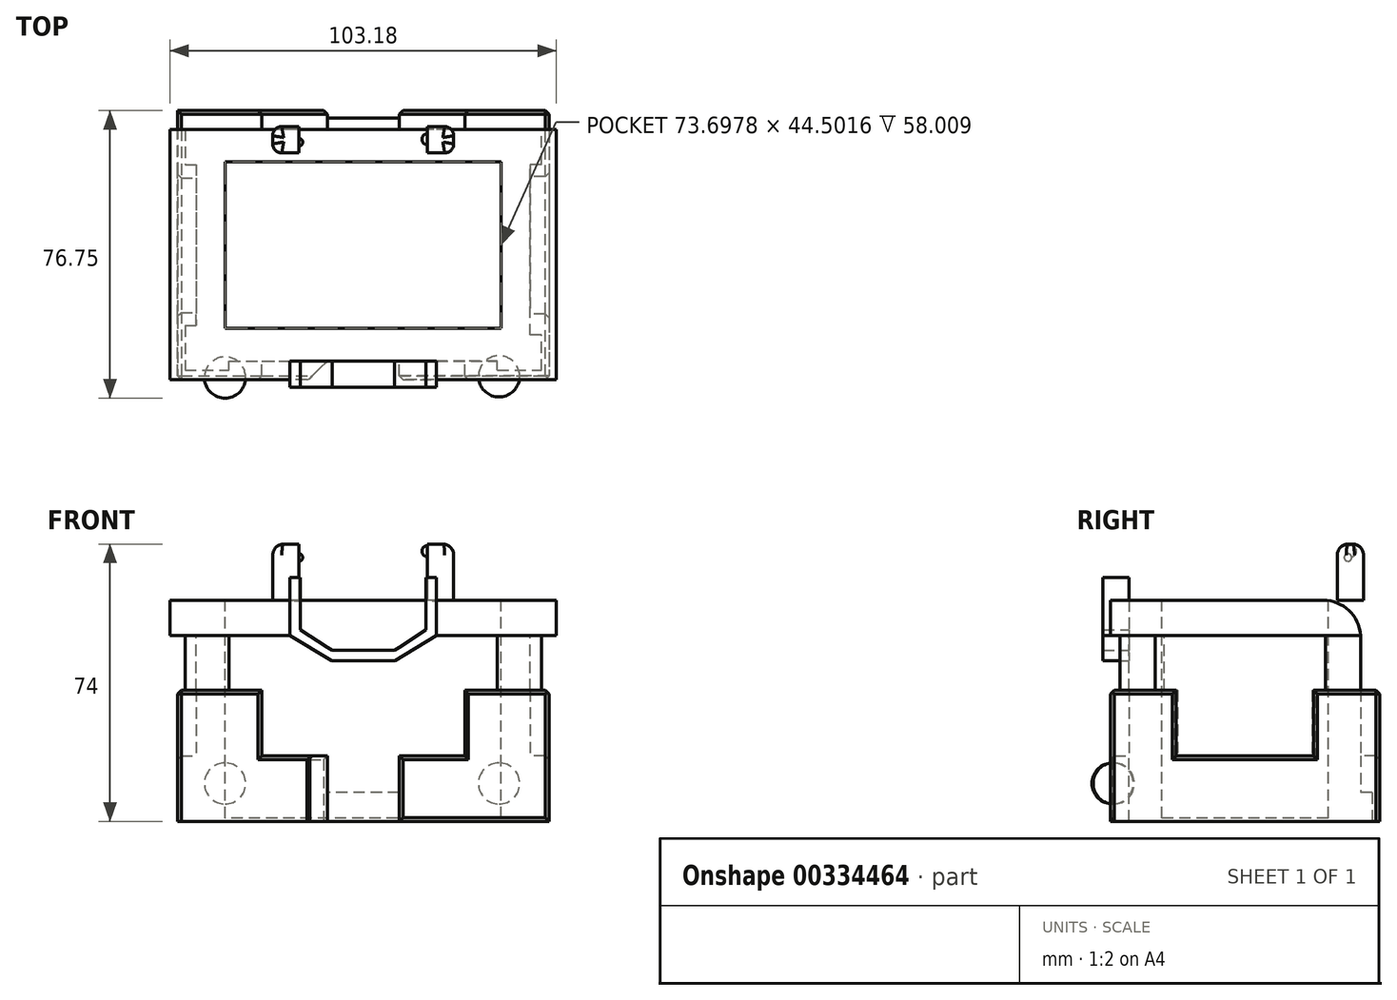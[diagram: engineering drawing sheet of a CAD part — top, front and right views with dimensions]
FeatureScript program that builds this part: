
annotation { "Feature Type Name" : "Feature", "Feature Type Description" : "" }
export const myFeature = defineFeature(function(context is Context, id is Id, definition is map)
    precondition{}
    {
        {
            var Q0;
            Q0=qCreatedBy(makeId("Top.planeOp"),FACE);
            var sketch = newSketch(context, id + "F0", { "sketchPlane" : qUnion([Q0])});
            skLineSegment(sketch, "E0.bottom", {"start": v(44.6, 30.9) * mm, "end": v(-44.6, 30.9) * mm});
            skLineSegment(sketch, "E0.top", {"start": v(44.6, -30.9) * mm, "end": v(-44.6, -30.9) * mm});
            skLineSegment(sketch, "E0.left", {"start": v(44.6, 30.9) * mm, "end": v(44.6, -30.9) * mm});
            skLineSegment(sketch, "E0.right", {"start": v(-44.6, 30.9) * mm, "end": v(-44.6, -30.9) * mm});
            skPoint(sketch, "E0.middle", {"position": v(0, 0) * mm});
            skSolve(sketch);
        }
        {
            var Q0;
            Q0 = qSketchRegion(id + "F0", true);
            extrude(context, id + "F1", {"entities" : qUnion([Q0]), "depth" : 59 * mm});
        }
        {
            var Q0;
            Q0=makeQuery(id+"F1.opExtrude","CAP_FACE",FACE,{"disambiguationData":[OSD([sQuery(id+"F0.wireOp",EDGE,"E0.bottom"),sQuery(id+"F0.wireOp",EDGE,"E0.top"),sQuery(id+"F0.wireOp",EDGE,"E0.left"),sQuery(id+"F0.wireOp",EDGE,"E0.right")])],"isStart":false});
            var sketch = newSketch(context, id + "F2", { "sketchPlane" : qUnion([Q0])});
            skLineSegment(sketch, "E1.bottom", {"start": v(36.85, 22.25) * mm, "end": v(-36.85, 22.25) * mm});
            skLineSegment(sketch, "E1.top", {"start": v(36.85, -22.25) * mm, "end": v(-36.85, -22.25) * mm});
            skLineSegment(sketch, "E1.left", {"start": v(36.85, 22.25) * mm, "end": v(36.85, -22.25) * mm});
            skLineSegment(sketch, "E1.right", {"start": v(-36.85, 22.25) * mm, "end": v(-36.85, -22.25) * mm});
            skPoint(sketch, "E1.middle", {"position": v(0, 0) * mm});
            skSolve(sketch);
        }
        {
            var Q0;
            Q0=makeQuery(id+"F2.imprint","IMPRINT",FACE,{"disambiguationData":[TD([[makeQuery(id+"F2.imprint","IMPRINT",EDGE,{"derivedFrom":sQuery(id+"F2.wireOp",EDGE,"E1.bottom")}),1.0]])]});
            extrude(context, id + "F3", {"entities" : qUnion([Q0]), "operationType" : NewBodyOperationType.REMOVE, "oppositeDirection" : true, "depth" : 58.1 * mm});
        }
        {
            var Q0;
            Q0=makeQuery(id+"F1.opExtrude","SWEPT_FACE",FACE,{"disambiguationData":[OSD([sQuery(id+"F0.wireOp",EDGE,"E0.top")])]});
            var sketch = newSketch(context, id + "F4", { "sketchPlane" : qUnion([Q0])});
            skLineSegment(sketch, "E2", {"start": v(-19.54, 65.05) * mm, "end": v(-19.54, 49.66) * mm});
            skLineSegment(sketch, "E3", {"start": v(-19.54, 49.66) * mm, "end": v(-8.44, 42.84) * mm});
            skLineSegment(sketch, "E4", {"start": v(-8.44, 42.84) * mm, "end": v(0, 42.84) * mm});
            skLineSegment(sketch, "E5.MirrorCS", {"start": v(8.44, 42.84) * mm, "end": v(0, 42.84) * mm});
            skLineSegment(sketch, "E6.MirrorCS", {"start": v(19.54, 49.66) * mm, "end": v(8.44, 42.84) * mm});
            skLineSegment(sketch, "E7.MirrorCS", {"start": v(19.54, 65.05) * mm, "end": v(19.54, 49.66) * mm});
            skLineSegment(sketch, "E8", {"start": v(-19.54, 65.05) * mm, "end": v(-16.74, 65.05) * mm});
            skLineSegment(sketch, "E9", {"start": v(-16.74, 65.05) * mm, "end": v(-16.74, 53.05) * mm});
            skLineSegment(sketch, "E10", {"start": v(-16.74, 53.05) * mm, "end": v(-16.74, 51.18) * mm});
            skLineSegment(sketch, "E11", {"start": v(-16.74, 51.18) * mm, "end": v(-9.6, 46.48) * mm});
            skLineSegment(sketch, "E12", {"start": v(-9.6, 46.48) * mm, "end": v(-8.32, 45.64) * mm});
            skLineSegment(sketch, "E13", {"start": v(-8.32, 45.64) * mm, "end": v(0, 45.64) * mm});
            skLineSegment(sketch, "E14.MirrorCS", {"start": v(8.32, 45.64) * mm, "end": v(0, 45.64) * mm});
            skLineSegment(sketch, "E15.MirrorCS", {"start": v(16.74, 51.18) * mm, "end": v(9.6, 46.48) * mm});
            skLineSegment(sketch, "E16.MirrorCS", {"start": v(9.6, 46.48) * mm, "end": v(8.32, 45.64) * mm});
            skLineSegment(sketch, "E17.MirrorCS", {"start": v(16.74, 65.05) * mm, "end": v(16.74, 53.05) * mm});
            skLineSegment(sketch, "E18.MirrorCS", {"start": v(16.74, 53.05) * mm, "end": v(16.74, 51.18) * mm});
            skLineSegment(sketch, "E19.MirrorCS", {"start": v(19.54, 65.05) * mm, "end": v(16.74, 65.05) * mm});
            skLineSegment(sketch, "E20.bottom", {"start": v(-44.6, 0) * mm, "end": v(-9.6, 0) * mm});
            skLineSegment(sketch, "E20.top", {"start": v(-44.6, 35) * mm, "end": v(-27.1, 35) * mm});
            skLineSegment(sketch, "E20.left", {"start": v(-44.6, 0) * mm, "end": v(-44.6, 35) * mm});
            skLineSegment(sketch, "E20.right", {"start": v(-9.6, 0) * mm, "end": v(-9.6, 17.5) * mm});
            skLineSegment(sketch, "E21.bottom", {"start": v(44.6, 0) * mm, "end": v(9.6, 0) * mm});
            skLineSegment(sketch, "E21.top", {"start": v(44.6, 35) * mm, "end": v(27.1, 35) * mm});
            skLineSegment(sketch, "E21.left", {"start": v(44.6, 0) * mm, "end": v(44.6, 35) * mm});
            skLineSegment(sketch, "E21.right", {"start": v(9.6, 0) * mm, "end": v(9.6, 17.5) * mm});
            skLineSegment(sketch, "E22", {"start": v(-27.1, 35) * mm, "end": v(-27.1, 17.5) * mm});
            skPoint(sketch, "E22.endSnap0", {"position": v(-9.6, 17.5) * mm});
            skLineSegment(sketch, "E23", {"start": v(-27.1, 17.5) * mm, "end": v(-9.6, 17.5) * mm});
            skLineSegment(sketch, "E24", {"start": v(27.1, 35) * mm, "end": v(27.1, 17.5) * mm});
            skLineSegment(sketch, "E25", {"start": v(27.1, 17.5) * mm, "end": v(9.6, 17.5) * mm});
            skPoint(sketch, "E26.orphan", {"position": v(9.6, 35) * mm});
            skPoint(sketch, "E27.orphan", {"position": v(-9.6, 35) * mm});
            skLineSegment(sketch, "E28", {"start": v(-9.6, 0) * mm, "end": v(9.6, 0) * mm});
            skLineSegment(sketch, "E29", {"start": v(-9.6, 7.65) * mm, "end": v(9.6, 7.65) * mm});
            skLineSegment(sketch, "E30", {"start": v(19.54, 49.66) * mm, "end": v(44.6, 49.66) * mm});
            skLineSegment(sketch, "E31", {"start": v(44.6, 49.66) * mm, "end": v(44.6, 59) * mm});
            skLineSegment(sketch, "E32", {"start": v(44.6, 59) * mm, "end": v(19.54, 59) * mm});
            skLineSegment(sketch, "E33", {"start": v(-44.6, 59) * mm, "end": v(-19.54, 59) * mm});
            skLineSegment(sketch, "E34", {"start": v(-19.54, 59) * mm, "end": v(-19.54, 49.66) * mm});
            skLineSegment(sketch, "E35", {"start": v(-44.6, 49.66) * mm, "end": v(-44.6, 59) * mm});
            skLineSegment(sketch, "E36", {"start": v(-44.6, 49.66) * mm, "end": v(-19.54, 49.66) * mm});
            skLineSegment(sketch, "E37", {"start": v(-35.84, 35) * mm, "end": v(-35.84, 49.66) * mm});
            skLineSegment(sketch, "E38", {"start": v(35.84, 35) * mm, "end": v(35.84, 49.66) * mm});
            skSolve(sketch);
        }
        {
            var Q0;
            {var subQ4=sQuery(id+"F4.wireOp",EDGE,"E21.bottom");Q0=makeQuery(id+"F4.imprint","IMPRINT",FACE,{"disambiguationData":[TD([[makeQuery(id+"F4.imprint","IMPRINT",EDGE,{"derivedFrom":subQ4}),-1.0]])]});}
            var Q1;
            {var subQ5=sQuery(id+"F4.wireOp",EDGE,"E20.bottom");Q1=makeQuery(id+"F4.imprint","IMPRINT",FACE,{"disambiguationData":[TD([[makeQuery(id+"F4.imprint","IMPRINT",EDGE,{"derivedFrom":subQ5}),-1.0]])]});}
            extrude(context, id + "F5", {"entities" : qUnion([Q0, Q1]), "operationType" : NewBodyOperationType.ADD, "depth" : 5 * mm});
        }
        {
            var Q0;
            Q0=makeQuery(id+"F4.imprint","IMPRINT",FACE,{"disambiguationData":[TD([[makeQuery(id+"F4.imprint","IMPRINT",EDGE,{"derivedFrom":sQuery(id+"F4.wireOp",EDGE,"E33")}),1.0]])]});
            var Q1;
            {var subQ0=sQuery(id+"F4.wireOp",EDGE,"E31");Q1=makeQuery(id+"F4.imprint","IMPRINT",FACE,{"disambiguationData":[TD([[makeQuery(id+"F4.imprint","IMPRINT",EDGE,{"derivedFrom":subQ0}),-1.0]])]});}
            extrude(context, id + "F6", {"entities" : qUnion([Q0, Q1]), "operationType" : NewBodyOperationType.ADD, "depth" : 5 * mm});
        }
        {
            var Q0;
            Q0=makeQuery(id+"F4.imprint","IMPRINT",FACE,{"disambiguationData":[TD([[makeQuery(id+"F4.imprint","IMPRINT",EDGE,{"derivedFrom":sQuery(id+"F4.wireOp",EDGE,"E3")}),1.0]])]});
            var Q1;
            {var subQ0=sQuery(id+"F4.wireOp",EDGE,"E2");Q1=makeQuery(id+"F4.imprint","IMPRINT",FACE,{"disambiguationData":[TD([[makeQuery(id+"F4.imprint","IMPRINT",EDGE,{"derivedFrom":subQ0}),1.0]])]});}
            var Q2;
            {var subQ0=sQuery(id+"F4.wireOp",EDGE,"E19.MirrorCS");Q2=makeQuery(id+"F4.imprint","IMPRINT",FACE,{"disambiguationData":[TD([[makeQuery(id+"F4.imprint","IMPRINT",EDGE,{"derivedFrom":subQ0}),1.0]])]});}
            extrude(context, id + "F7", {"entities" : qUnion([Q0, Q1, Q2]), "operationType" : NewBodyOperationType.ADD, "depth" : 7 * mm});
        }
        {
            var Q0;
            Q0=makeQuery(id+"F1.opExtrude","SWEPT_FACE",FACE,{"disambiguationData":[OSD([sQuery(id+"F0.wireOp",EDGE,"E0.bottom")])]});
            var sketch = newSketch(context, id + "F8", { "sketchPlane" : qUnion([Q0])});
            skLineSegment(sketch, "E39.0.0", {"start": v(-9.6, 17.5) * mm, "end": v(-9.6, 0) * mm});
            skLineSegment(sketch, "E39.0.1", {"start": v(-9.6, 0) * mm, "end": v(-44.6, 0) * mm});
            skLineSegment(sketch, "E39.0.2", {"start": v(-44.6, 0) * mm, "end": v(-44.6, 35) * mm});
            skLineSegment(sketch, "E39.0.3", {"start": v(-44.6, 35) * mm, "end": v(-27.1, 35) * mm});
            skLineSegment(sketch, "E39.0.4", {"start": v(-27.1, 35) * mm, "end": v(-27.1, 17.5) * mm});
            skLineSegment(sketch, "E39.0.5", {"start": v(-27.1, 17.5) * mm, "end": v(-9.6, 17.5) * mm});
            skLineSegment(sketch, "E40.0.0", {"start": v(-35.84, 49.66) * mm, "end": v(-35.84, 35) * mm});
            skLineSegment(sketch, "E40.0.1", {"start": v(-35.84, 35) * mm, "end": v(-44.6, 35) * mm});
            skLineSegment(sketch, "E40.0.2", {"start": v(-44.6, 35) * mm, "end": v(-44.6, 49.66) * mm});
            skLineSegment(sketch, "E40.0.3", {"start": v(-44.6, 49.66) * mm, "end": v(-35.84, 49.66) * mm});
            skLineSegment(sketch, "E41.0.0", {"start": v(-19.54, 59) * mm, "end": v(-19.54, 49.66) * mm});
            skLineSegment(sketch, "E41.0.1", {"start": v(-19.54, 49.66) * mm, "end": v(-44.6, 49.66) * mm});
            skLineSegment(sketch, "E41.0.2", {"start": v(-44.6, 49.66) * mm, "end": v(-44.6, 59) * mm});
            skLineSegment(sketch, "E41.0.3", {"start": v(-44.6, 59) * mm, "end": v(-19.54, 59) * mm});
            skLineSegment(sketch, "E42.0.0", {"start": v(-19.54, 49.66) * mm, "end": v(-19.54, 65.05) * mm});
            skLineSegment(sketch, "E42.0.1", {"start": v(-19.54, 65.05) * mm, "end": v(-16.74, 65.05) * mm});
            skLineSegment(sketch, "E42.0.2", {"start": v(-16.74, 65.05) * mm, "end": v(-16.74, 51.18) * mm});
            skLineSegment(sketch, "E42.0.3", {"start": v(-16.74, 51.18) * mm, "end": v(-9.6, 46.48) * mm});
            skLineSegment(sketch, "E42.0.4", {"start": v(-9.6, 46.48) * mm, "end": v(-8.32, 45.64) * mm});
            skLineSegment(sketch, "E42.0.5", {"start": v(-8.32, 45.64) * mm, "end": v(8.32, 45.64) * mm});
            skLineSegment(sketch, "E42.0.6", {"start": v(8.32, 45.64) * mm, "end": v(9.6, 46.48) * mm});
            skLineSegment(sketch, "E42.0.7", {"start": v(9.6, 46.48) * mm, "end": v(16.74, 51.18) * mm});
            skLineSegment(sketch, "E42.0.8", {"start": v(16.74, 51.18) * mm, "end": v(16.74, 65.05) * mm});
            skLineSegment(sketch, "E42.0.9", {"start": v(16.74, 65.05) * mm, "end": v(19.54, 65.05) * mm});
            skLineSegment(sketch, "E42.0.10", {"start": v(19.54, 65.05) * mm, "end": v(19.54, 49.66) * mm});
            skLineSegment(sketch, "E42.0.11", {"start": v(19.54, 49.66) * mm, "end": v(8.44, 42.84) * mm});
            skLineSegment(sketch, "E42.0.12", {"start": v(8.44, 42.84) * mm, "end": v(-8.44, 42.84) * mm});
            skLineSegment(sketch, "E42.0.13", {"start": v(-8.44, 42.84) * mm, "end": v(-19.54, 49.66) * mm});
            skLineSegment(sketch, "E43.0.0", {"start": v(44.6, 59) * mm, "end": v(44.6, 49.66) * mm});
            skLineSegment(sketch, "E43.0.1", {"start": v(44.6, 49.66) * mm, "end": v(19.54, 49.66) * mm});
            skLineSegment(sketch, "E43.0.2", {"start": v(19.54, 49.66) * mm, "end": v(19.54, 59) * mm});
            skLineSegment(sketch, "E43.0.3", {"start": v(19.54, 59) * mm, "end": v(44.6, 59) * mm});
            skLineSegment(sketch, "E44.0.0", {"start": v(44.6, 35) * mm, "end": v(35.84, 35) * mm});
            skLineSegment(sketch, "E44.0.1", {"start": v(35.84, 35) * mm, "end": v(35.84, 49.66) * mm});
            skLineSegment(sketch, "E44.0.2", {"start": v(35.84, 49.66) * mm, "end": v(44.6, 49.66) * mm});
            skLineSegment(sketch, "E44.0.3", {"start": v(44.6, 49.66) * mm, "end": v(44.6, 35) * mm});
            skLineSegment(sketch, "E45.0.0", {"start": v(44.6, 0) * mm, "end": v(9.6, 0) * mm});
            skLineSegment(sketch, "E45.0.1", {"start": v(9.6, 0) * mm, "end": v(9.6, 17.5) * mm});
            skLineSegment(sketch, "E45.0.2", {"start": v(9.6, 17.5) * mm, "end": v(27.1, 17.5) * mm});
            skLineSegment(sketch, "E45.0.3", {"start": v(27.1, 17.5) * mm, "end": v(27.1, 35) * mm});
            skLineSegment(sketch, "E45.0.4", {"start": v(27.1, 35) * mm, "end": v(44.6, 35) * mm});
            skLineSegment(sketch, "E45.0.5", {"start": v(44.6, 35) * mm, "end": v(44.6, 0) * mm});
            skLineSegment(sketch, "E46.0.0", {"start": v(-9.6, 7.65) * mm, "end": v(9.6, 7.65) * mm});
            skLineSegment(sketch, "E46.0.1", {"start": v(9.6, 7.65) * mm, "end": v(9.6, 0) * mm});
            skLineSegment(sketch, "E46.0.2", {"start": v(9.6, 0) * mm, "end": v(-9.6, 0) * mm});
            skLineSegment(sketch, "E46.0.3", {"start": v(-9.6, 0) * mm, "end": v(-9.6, 7.65) * mm});
            skLineSegment(sketch, "E47", {"start": v(0, 0) * mm, "end": v(0, 73.71) * mm});
            skArc(sketch, "E48", {"start": v(-63.35, 14.4) * mm, "mid": v(-68.85, 8.9) * mm, "end": v(-63.35, 3.4) * mm});
            skArc(sketch, "E49", {"start": v(55.37, 14.4) * mm, "mid": v(49.87, 8.9) * mm, "end": v(55.37, 3.4) * mm});
            skLineSegment(sketch, "E50", {"start": v(-63.35, 3.4) * mm, "end": v(-63.35, 14.4) * mm});
            skLineSegment(sketch, "E51", {"start": v(55.37, 3.4) * mm, "end": v(55.37, 14.4) * mm});
            skSolve(sketch);
        }
        {
            var Q0;
            Q0=makeQuery(id+"F8.imprint","IMPRINT",FACE,{"disambiguationData":[TD([[makeQuery(id+"F8.imprint","IMPRINT",EDGE,{"derivedFrom":sQuery(id+"F8.wireOp",EDGE,"E45.0.0")}),1.0]])]});
            var Q1;
            Q1=makeQuery(id+"F8.imprint","IMPRINT",FACE,{"disambiguationData":[TD([[makeQuery(id+"F8.imprint","IMPRINT",EDGE,{"derivedFrom":sQuery(id+"F8.wireOp",EDGE,"E39.0.0")}),-1.0]])]});
            extrude(context, id + "F9", {"entities" : qUnion([Q0, Q1]), "operationType" : NewBodyOperationType.ADD, "depth" : 5 * mm});
        }
        {
            var Q0;
            Q0=makeQuery(id+"F8.imprint","IMPRINT",FACE,{"disambiguationData":[TD([[makeQuery(id+"F8.imprint","IMPRINT",EDGE,{"derivedFrom":sQuery(id+"F8.wireOp",EDGE,"E46.0.0")}),-1.0]])]});
            extrude(context, id + "F10", {"entities" : qUnion([Q0]), "operationType" : NewBodyOperationType.ADD, "depth" : 3 * mm});
        }
        {
            var Q0;
            {var subQ3=sQuery(id+"F4.wireOp",EDGE,"E37");Q0=makeQuery(id+"F4.imprint","IMPRINT",FACE,{"disambiguationData":[TD([[makeQuery(id+"F4.imprint","IMPRINT",EDGE,{"derivedFrom":subQ3}),1.0]])]});}
            var Q1;
            {var subQ3=sQuery(id+"F4.wireOp",EDGE,"E38");Q1=makeQuery(id+"F4.imprint","IMPRINT",FACE,{"disambiguationData":[TD([[makeQuery(id+"F4.imprint","IMPRINT",EDGE,{"derivedFrom":subQ3}),-1.0]])]});}
            extrude(context, id + "F11", {"entities" : qUnion([Q0, Q1]), "operationType" : NewBodyOperationType.ADD, "depth" : 2.5 * mm});
        }
        {
            var Q0;
            {var subQ0=sQuery(id+"F0.wireOp",EDGE,"E0.right");Q0=makeQuery(id+"F11.boolean.opBoolean","MERGE",FACE,{"derivedFrom":[makeQuery(id+"F9.boolean.opBoolean","MERGE",FACE,{"derivedFrom":[makeQuery(id+"F6.boolean.opBoolean","MERGE",FACE,{"derivedFrom":[makeQuery(id+"F5.boolean.opBoolean","MERGE",FACE,{"derivedFrom":[makeQuery(id+"F1.opExtrude","SWEPT_FACE",FACE,{"disambiguationData":[OSD([subQ0])]}),makeQuery(id+"F5.opExtrude","SWEPT_FACE",FACE,{"disambiguationData":[OSD([sQuery(id+"F4.wireOp",EDGE,"E20.left")])]})]}),makeQuery(id+"F6.opExtrude","SWEPT_FACE",FACE,{"disambiguationData":[OSD([sQuery(id+"F4.wireOp",EDGE,"E35")])]})]}),makeQuery(id+"F9.opExtrude","SWEPT_FACE",FACE,{"disambiguationData":[OSD([sQuery(id+"F8.wireOp",EDGE,"E45.0.5")])]})]}),makeQuery(id+"F11.opExtrude","SWEPT_FACE",FACE,{"disambiguationData":[OSD([sQuery(id+"F0.wireOp",EDGE,"E0.top"),subQ0])]})]});}
            var sketch = newSketch(context, id + "F12", { "sketchPlane" : qUnion([Q0])});
            skLineSegment(sketch, "E52", {"start": v(-35.9, 35) * mm, "end": v(-35.9, 0) * mm});
            skLineSegment(sketch, "E53", {"start": v(-35.9, 0) * mm, "end": v(-0.9, 0) * mm});
            skLineSegment(sketch, "E54", {"start": v(-35.9, 35) * mm, "end": v(-17.95, 35) * mm});
            skLineSegment(sketch, "E55", {"start": v(0, 17.5) * mm, "end": v(0, 0) * mm});
            skLineSegment(sketch, "E56", {"start": v(-17.95, 35) * mm, "end": v(-17.95, 17.5) * mm});
            skLineSegment(sketch, "E57", {"start": v(-17.95, 17.5) * mm, "end": v(0, 17.5) * mm});
            skPoint(sketch, "E58.orphan", {"position": v(0, 35) * mm});
            skLineSegment(sketch, "E59.MirrorCS", {"start": v(35.9, 35) * mm, "end": v(17.95, 35) * mm});
            skLineSegment(sketch, "E60.MirrorCS", {"start": v(17.95, 35) * mm, "end": v(17.95, 17.5) * mm});
            skLineSegment(sketch, "E61.MirrorCS", {"start": v(17.95, 17.5) * mm, "end": v(0, 17.5) * mm});
            skLineSegment(sketch, "E62.MirrorCS", {"start": v(35.9, 0) * mm, "end": v(0.9, 0) * mm});
            skLineSegment(sketch, "E63.MirrorCS", {"start": v(35.9, 35) * mm, "end": v(35.9, 0) * mm});
            skLineSegment(sketch, "E64", {"start": v(35.9, 49.66) * mm, "end": v(35.9, 59) * mm});
            skLineSegment(sketch, "E65", {"start": v(35.9, 59) * mm, "end": v(-30.9, 59) * mm});
            skLineSegment(sketch, "E66", {"start": v(-30.9, 59) * mm, "end": v(-30.9, 49.66) * mm});
            skLineSegment(sketch, "E67", {"start": v(-30.9, 49.66) * mm, "end": v(35.9, 49.66) * mm});
            skLineSegment(sketch, "E68", {"start": v(-21.5, 35) * mm, "end": v(-21.5, 49.66) * mm});
            skLineSegment(sketch, "E69.MirrorCS", {"start": v(21.5, 35) * mm, "end": v(21.5, 49.66) * mm});
            skSolve(sketch);
        }
        {
            var Q0;
            {var subQ4=sQuery(id+"F12.wireOp",EDGE,"E64");Q0=makeQuery(id+"F12.imprint","IMPRINT",FACE,{"disambiguationData":[TD([[makeQuery(id+"F12.imprint","IMPRINT",EDGE,{"derivedFrom":subQ4}),-1.0]])]});}
            extrude(context, id + "F13", {"entities" : qUnion([Q0]), "operationType" : NewBodyOperationType.ADD, "depth" : 7 * mm});
        }
        {
            var Q0;
            {var subQ3=sQuery(id+"F12.wireOp",EDGE,"E68");Q0=makeQuery(id+"F12.imprint","IMPRINT",FACE,{"disambiguationData":[TD([[makeQuery(id+"F12.imprint","IMPRINT",EDGE,{"derivedFrom":subQ3}),1.0]])]});}
            var Q1;
            {var subQ2=sQuery(id+"F12.wireOp",EDGE,"E69.MirrorCS");Q1=makeQuery(id+"F12.imprint","IMPRINT",FACE,{"disambiguationData":[TD([[makeQuery(id+"F12.imprint","IMPRINT",EDGE,{"derivedFrom":subQ2}),-1.0]])]});}
            extrude(context, id + "F14", {"entities" : qUnion([Q0, Q1]), "operationType" : NewBodyOperationType.ADD, "depth" : 3 * mm});
        }
        {
            var Q0;
            {var subQ6=sQuery(id+"F12.wireOp",EDGE,"E52");Q0=makeQuery(id+"F12.imprint","IMPRINT",FACE,{"disambiguationData":[TD([[makeQuery(id+"F12.imprint","IMPRINT",EDGE,{"derivedFrom":subQ6}),1.0]])]});}
            var Q1;
            {var subQ6=sQuery(id+"F12.wireOp",EDGE,"E55");Q1=makeQuery(id+"F12.imprint","IMPRINT",FACE,{"disambiguationData":[TD([[makeQuery(id+"F12.imprint","IMPRINT",EDGE,{"derivedFrom":subQ6}),1.0]])]});}
            extrude(context, id + "F15", {"entities" : qUnion([Q0, Q1]), "operationType" : NewBodyOperationType.ADD, "depth" : 5 * mm});
        }
        {
            var Q0;
            {var subQ0=sQuery(id+"F0.wireOp",EDGE,"E0.left");Q0=makeQuery(id+"F11.boolean.opBoolean","MERGE",FACE,{"derivedFrom":[makeQuery(id+"F9.boolean.opBoolean","MERGE",FACE,{"derivedFrom":[makeQuery(id+"F6.boolean.opBoolean","MERGE",FACE,{"derivedFrom":[makeQuery(id+"F5.boolean.opBoolean","MERGE",FACE,{"derivedFrom":[makeQuery(id+"F1.opExtrude","SWEPT_FACE",FACE,{"disambiguationData":[OSD([subQ0])]}),makeQuery(id+"F5.opExtrude","SWEPT_FACE",FACE,{"disambiguationData":[OSD([sQuery(id+"F4.wireOp",EDGE,"E21.left")])]})]}),makeQuery(id+"F6.opExtrude","SWEPT_FACE",FACE,{"disambiguationData":[OSD([sQuery(id+"F4.wireOp",EDGE,"E31")])]})]}),makeQuery(id+"F9.opExtrude","SWEPT_FACE",FACE,{"disambiguationData":[OSD([sQuery(id+"F8.wireOp",EDGE,"E39.0.2")])]})]}),makeQuery(id+"F11.opExtrude","SWEPT_FACE",FACE,{"disambiguationData":[OSD([sQuery(id+"F0.wireOp",EDGE,"E0.top"),subQ0])]})]});}
            var sketch = newSketch(context, id + "F16", { "sketchPlane" : qUnion([Q0])});
            skLineSegment(sketch, "E70.bottom", {"start": v(-35.9, 0) * mm, "end": v(-0.9, 0) * mm});
            skLineSegment(sketch, "E70.top", {"start": v(-35.9, 35) * mm, "end": v(-18.4, 35) * mm});
            skLineSegment(sketch, "E70.left", {"start": v(-35.9, 0) * mm, "end": v(-35.9, 35) * mm});
            skLineSegment(sketch, "E71.bottom", {"start": v(35.9, 0) * mm, "end": v(0.9, 0) * mm});
            skLineSegment(sketch, "E71.top", {"start": v(35.9, 35) * mm, "end": v(18.29, 35) * mm});
            skLineSegment(sketch, "E71.left", {"start": v(35.9, 0) * mm, "end": v(35.9, 35) * mm});
            skLineSegment(sketch, "E72", {"start": v(-18.4, 35) * mm, "end": v(-18.4, 17.5) * mm});
            skPoint(sketch, "E72.endSnap0", {"position": v(-0.9, 17.5) * mm});
            skLineSegment(sketch, "E73", {"start": v(-18.4, 17.5) * mm, "end": v(-0.9, 17.5) * mm});
            skLineSegment(sketch, "E74", {"start": v(18.29, 17.5) * mm, "end": v(18.29, 35) * mm});
            skLineSegment(sketch, "E75", {"start": v(18.29, 17.5) * mm, "end": v(0, 17.5) * mm});
            skPoint(sketch, "E76.orphan", {"position": v(-0.9, 35) * mm});
            skLineSegment(sketch, "E77", {"start": v(-0.9, 17.5) * mm, "end": v(0.9, 17.5) * mm});
            skLineSegment(sketch, "E78", {"start": v(-0.9, 0) * mm, "end": v(0.9, 0) * mm});
            skLineSegment(sketch, "E79", {"start": v(-33.4, 49.66) * mm, "end": v(30.9, 49.66) * mm});
            skLineSegment(sketch, "E80", {"start": v(21.5, 35) * mm, "end": v(21.5, 49.66) * mm});
            skLineSegment(sketch, "E81", {"start": v(-24, 35) * mm, "end": v(-24, 49.66) * mm});
            skSolve(sketch);
        }
        {
            var Q0;
            {var subQ6=sQuery(id+"F4.wireOp",EDGE,"E31");Q0=makeQuery(id+"F16.imprint","IMPRINT",FACE,{"disambiguationData":[TD([[makeQuery(id+"F16.imprint","IMPRINT",EDGE,{"derivedFrom":makeQuery(id+"F6.opExtrude","CAP_EDGE",EDGE,{"disambiguationData":[OSD([subQ6])],"isStart":false})}),1.0]])]});}
            extrude(context, id + "F17", {"entities" : qUnion([Q0]), "operationType" : NewBodyOperationType.ADD, "depth" : 7 * mm});
        }
        {
            var Q0;
            Q0=makeQuery(id+"F16.imprint","IMPRINT",FACE,{"disambiguationData":[TD([[makeQuery(id+"F16.imprint","IMPRINT",EDGE,{"derivedFrom":sQuery(id+"F16.wireOp",EDGE,"E70.bottom")}),-1.0]])]});
            extrude(context, id + "F18", {"entities" : qUnion([Q0]), "operationType" : NewBodyOperationType.ADD, "depth" : 5 * mm});
        }
        {
            var Q0;
            {var subQ3=sQuery(id+"F16.wireOp",EDGE,"E80");Q0=makeQuery(id+"F16.imprint","IMPRINT",FACE,{"disambiguationData":[TD([[makeQuery(id+"F16.imprint","IMPRINT",EDGE,{"derivedFrom":subQ3}),-1.0]])]});}
            var Q1;
            {var subQ4=sQuery(id+"F16.wireOp",EDGE,"E81");Q1=makeQuery(id+"F16.imprint","IMPRINT",FACE,{"disambiguationData":[TD([[makeQuery(id+"F16.imprint","IMPRINT",EDGE,{"derivedFrom":subQ4}),1.0]])]});}
            extrude(context, id + "F19", {"entities" : qUnion([Q0, Q1]), "operationType" : NewBodyOperationType.ADD, "depth" : 3 * mm});
        }
        {
            var Q0;
            Q0=makeQuery(id+"F8.imprint","IMPRINT",FACE,{"disambiguationData":[TD([[makeQuery(id+"F8.imprint","IMPRINT",EDGE,{"derivedFrom":sQuery(id+"F8.wireOp",EDGE,"E48")}),1.0]])]});
            var Q1;
            Q1=sQuery(id+"F8.wireOp",EDGE,"E50");
            revolve(context, id + "F20", {"entities" : qUnion([Q0]), "axis" : qUnion([Q1]), "revolveType" : RevolveType.FULL});
        }
        {
            var Q0;
            Q0=makeQuery(id+"F8.imprint","IMPRINT",FACE,{"disambiguationData":[TD([[makeQuery(id+"F8.imprint","IMPRINT",EDGE,{"derivedFrom":sQuery(id+"F8.wireOp",EDGE,"E49")}),1.0]])]});
            var Q1;
            Q1=sQuery(id+"F8.wireOp",EDGE,"E51");
            revolve(context, id + "F21", {"entities" : qUnion([Q0]), "axis" : qUnion([Q1]), "revolveType" : RevolveType.FULL});
        }
        {
            var Q0;
            Q0=makeQuery(id+"F20.opRevolve","SWEPT_BODY",BODY,{"disambiguationData":[OSD([sQuery(id+"F8.wireOp",EDGE,"E48"),sQuery(id+"F8.wireOp",EDGE,"E50")])]});
            transform(context, id + "F22", {"entities" : qUnion([Q0]), "transformType" : TransformType.TRANSLATION_3D, "dx" : -27.1 * mm, "dy" : -65.95 * mm, "dz" : 1.2 * mm, "makeCopy" : false});
        }
        {
            var Q0;
            Q0=makeQuery(id+"F21.opRevolve","SWEPT_BODY",BODY,{"disambiguationData":[OSD([sQuery(id+"F8.wireOp",EDGE,"E49"),sQuery(id+"F8.wireOp",EDGE,"E51")])]});
            transform(context, id + "F23", {"entities" : qUnion([Q0]), "transformType" : TransformType.TRANSLATION_3D, "dx" : 18.48 * mm, "dy" : -66.25 * mm, "dz" : 1.2 * mm, "makeCopy" : false});
        }
        {
            var Q0;
            Q0=makeQuery(id+"F18.opExtrude","CAP_EDGE",EDGE,{"disambiguationData":[OSD([sQuery(id+"F16.wireOp",EDGE,"E70.left")])],"isStart":false});
            var Q1;
            Q1=makeQuery(id+"F18.boolean.opBoolean","MERGE",EDGE,{"derivedFrom":[makeQuery(id+"F5.opExtrude","CAP_EDGE",EDGE,{"disambiguationData":[OSD([sQuery(id+"F4.wireOp",EDGE,"E21.top")])],"isStart":false}),makeQuery(id+"F18.opExtrude","SWEPT_EDGE",EDGE,{"disambiguationData":[OSD([sQuery(id+"F16.wireOp",EDGE,"E70.top"),sQuery(id+"F16.wireOp",EDGE,"E70.left")])]})]});
            var Q2;
            Q2=makeQuery(id+"F5.opExtrude","CAP_EDGE",EDGE,{"disambiguationData":[OSD([sQuery(id+"F4.wireOp",EDGE,"E24")])],"isStart":false});
            var Q3;
            Q3=makeQuery(id+"F18.boolean.opBoolean","MERGE",FACE,{"derivedFrom":[makeQuery(id+"F5.opExtrude","CAP_FACE",FACE,{"disambiguationData":[OSD([sQuery(id+"F4.wireOp",EDGE,"E21.bottom"),sQuery(id+"F4.wireOp",EDGE,"E21.top"),sQuery(id+"F4.wireOp",EDGE,"E21.left"),sQuery(id+"F4.wireOp",EDGE,"E21.right"),sQuery(id+"F4.wireOp",EDGE,"E24"),sQuery(id+"F4.wireOp",EDGE,"E25")])],"isStart":false}),makeQuery(id+"F18.opExtrude","SWEPT_FACE",FACE,{"disambiguationData":[OSD([sQuery(id+"F16.wireOp",EDGE,"E70.left")])]})]});
            chamfer(context, id + "F24", {"entities" : qUnion([Q0, Q1, Q2, Q3]), "width" : 1 * mm, "tangentPropagation" : true});
        }
        {
            var Q0;
            Q0=makeQuery(id+"F5.opExtrude","CAP_EDGE",EDGE,{"disambiguationData":[OSD([sQuery(id+"F4.wireOp",EDGE,"E20.right")])],"isStart":false});
            chamfer(context, id + "F25", {"entities" : qUnion([Q0]), "width" : 5 * mm, "tangentPropagation" : true});
        }
        {
            var Q0;
            Q0=makeQuery(id+"F5.opExtrude","CAP_EDGE",EDGE,{"disambiguationData":[OSD([sQuery(id+"F4.wireOp",EDGE,"E23")])],"isStart":false});
            var Q1;
            Q1=makeQuery(id+"F15.boolean.opBoolean","MERGE",EDGE,{"derivedFrom":[makeQuery(id+"F5.opExtrude","CAP_EDGE",EDGE,{"disambiguationData":[OSD([sQuery(id+"F4.wireOp",EDGE,"E20.top")])],"isStart":false}),makeQuery(id+"F15.opExtrude","SWEPT_EDGE",EDGE,{"disambiguationData":[OSD([sQuery(id+"F12.wireOp",EDGE,"E59.MirrorCS"),sQuery(id+"F12.wireOp",EDGE,"E63.MirrorCS")])]})]});
            var Q2;
            Q2=makeQuery(id+"F5.opExtrude","CAP_EDGE",EDGE,{"disambiguationData":[OSD([sQuery(id+"F4.wireOp",EDGE,"E22")])],"isStart":false});
            var Q3;
            {var subQ0=sQuery(id+"F4.wireOp",EDGE,"E20.right");Q3=makeQuery(id+"F25.opChamfer","BLEND_EDGE",EDGE,{"blendedFrom":[makeQuery(id+"F5.opExtrude","CAP_EDGE",EDGE,{"disambiguationData":[OSD([subQ0])],"isStart":false}),makeQuery(id+"F15.boolean.opBoolean","MERGE",FACE,{"derivedFrom":[makeQuery(id+"F5.opExtrude","CAP_FACE",FACE,{"disambiguationData":[OSD([sQuery(id+"F4.wireOp",EDGE,"E20.bottom"),sQuery(id+"F4.wireOp",EDGE,"E20.top"),sQuery(id+"F4.wireOp",EDGE,"E20.left"),subQ0,sQuery(id+"F4.wireOp",EDGE,"E22"),sQuery(id+"F4.wireOp",EDGE,"E23")])],"isStart":false}),makeQuery(id+"F15.opExtrude","SWEPT_FACE",FACE,{"disambiguationData":[OSD([sQuery(id+"F12.wireOp",EDGE,"E63.MirrorCS")])]})]})],"blendedInto":[makeQuery(id+"F15.boolean.opBoolean","MERGE",FACE,{"derivedFrom":[makeQuery(id+"F5.opExtrude","CAP_FACE",FACE,{"disambiguationData":[OSD([sQuery(id+"F4.wireOp",EDGE,"E20.bottom"),sQuery(id+"F4.wireOp",EDGE,"E20.top"),sQuery(id+"F4.wireOp",EDGE,"E20.left"),subQ0,sQuery(id+"F4.wireOp",EDGE,"E22"),sQuery(id+"F4.wireOp",EDGE,"E23")])],"isStart":false}),makeQuery(id+"F15.opExtrude","SWEPT_FACE",FACE,{"disambiguationData":[OSD([sQuery(id+"F12.wireOp",EDGE,"E63.MirrorCS")])]})]})]});}
            var Q4;
            Q4=makeQuery(id+"F15.opExtrude","CAP_EDGE",EDGE,{"disambiguationData":[OSD([sQuery(id+"F12.wireOp",EDGE,"E63.MirrorCS")])],"isStart":false});
            var Q5;
            Q5=makeQuery(id+"F15.opExtrude","CAP_EDGE",EDGE,{"disambiguationData":[OSD([sQuery(id+"F12.wireOp",EDGE,"E59.MirrorCS")])],"isStart":false});
            var Q6;
            Q6=makeQuery(id+"F15.opExtrude","CAP_EDGE",EDGE,{"disambiguationData":[OSD([sQuery(id+"F12.wireOp",EDGE,"E60.MirrorCS")])],"isStart":false});
            var Q7;
            Q7=makeQuery(id+"F15.opExtrude","CAP_EDGE",EDGE,{"disambiguationData":[OSD([sQuery(id+"F12.wireOp",EDGE,"E57"),sQuery(id+"F12.wireOp",EDGE,"E61.MirrorCS")])],"isStart":false});
            var Q8;
            Q8=makeQuery(id+"F15.opExtrude","CAP_EDGE",EDGE,{"disambiguationData":[OSD([sQuery(id+"F12.wireOp",EDGE,"E56")])],"isStart":false});
            var Q9;
            Q9=makeQuery(id+"F15.opExtrude","CAP_EDGE",EDGE,{"disambiguationData":[OSD([sQuery(id+"F12.wireOp",EDGE,"E54")])],"isStart":false});
            var Q10;
            Q10=makeQuery(id+"F15.boolean.opBoolean","MERGE",EDGE,{"derivedFrom":[makeQuery(id+"F9.opExtrude","CAP_EDGE",EDGE,{"disambiguationData":[OSD([sQuery(id+"F8.wireOp",EDGE,"E45.0.4")])],"isStart":false}),makeQuery(id+"F15.opExtrude","SWEPT_EDGE",EDGE,{"disambiguationData":[OSD([sQuery(id+"F12.wireOp",EDGE,"E52"),sQuery(id+"F12.wireOp",EDGE,"E54")])]})]});
            var Q11;
            Q11=makeQuery(id+"F9.opExtrude","CAP_EDGE",EDGE,{"disambiguationData":[OSD([sQuery(id+"F8.wireOp",EDGE,"E45.0.3")])],"isStart":false});
            var Q12;
            Q12=makeQuery(id+"F9.opExtrude","CAP_EDGE",EDGE,{"disambiguationData":[OSD([sQuery(id+"F8.wireOp",EDGE,"E45.0.2")])],"isStart":false});
            var Q13;
            Q13=makeQuery(id+"F9.opExtrude","CAP_EDGE",EDGE,{"disambiguationData":[OSD([sQuery(id+"F8.wireOp",EDGE,"E45.0.1"),sQuery(id+"F8.wireOp",EDGE,"E46.0.1")])],"isStart":false});
            var Q14;
            Q14=makeQuery(id+"F9.opExtrude","CAP_EDGE",EDGE,{"disambiguationData":[OSD([sQuery(id+"F8.wireOp",EDGE,"E39.0.0"),sQuery(id+"F8.wireOp",EDGE,"E46.0.3")])],"isStart":false});
            var Q15;
            Q15=makeQuery(id+"F9.opExtrude","CAP_EDGE",EDGE,{"disambiguationData":[OSD([sQuery(id+"F8.wireOp",EDGE,"E39.0.5")])],"isStart":false});
            var Q16;
            Q16=makeQuery(id+"F9.opExtrude","CAP_EDGE",EDGE,{"disambiguationData":[OSD([sQuery(id+"F8.wireOp",EDGE,"E39.0.4")])],"isStart":false});
            var Q17;
            Q17=makeQuery(id+"F18.boolean.opBoolean","MERGE",EDGE,{"derivedFrom":[makeQuery(id+"F9.opExtrude","CAP_EDGE",EDGE,{"disambiguationData":[OSD([sQuery(id+"F8.wireOp",EDGE,"E39.0.3"),sQuery(id+"F8.wireOp",EDGE,"E40.0.1")])],"isStart":false}),makeQuery(id+"F18.opExtrude","SWEPT_EDGE",EDGE,{"disambiguationData":[OSD([sQuery(id+"F16.wireOp",EDGE,"E71.top"),sQuery(id+"F16.wireOp",EDGE,"E71.left")])]})]});
            var Q18;
            Q18=makeQuery(id+"F18.opExtrude","CAP_EDGE",EDGE,{"disambiguationData":[OSD([sQuery(id+"F16.wireOp",EDGE,"E71.left")])],"isStart":false});
            var Q19;
            Q19=makeQuery(id+"F18.opExtrude","CAP_EDGE",EDGE,{"disambiguationData":[OSD([sQuery(id+"F16.wireOp",EDGE,"E71.top")])],"isStart":false});
            var Q20;
            Q20=makeQuery(id+"F18.opExtrude","CAP_EDGE",EDGE,{"disambiguationData":[OSD([sQuery(id+"F16.wireOp",EDGE,"E74")])],"isStart":false});
            var Q21;
            Q21=makeQuery(id+"F18.opExtrude","CAP_EDGE",EDGE,{"disambiguationData":[OSD([sQuery(id+"F16.wireOp",EDGE,"E73"),sQuery(id+"F16.wireOp",EDGE,"E75"),sQuery(id+"F16.wireOp",EDGE,"E77")])],"isStart":false});
            var Q22;
            Q22=makeQuery(id+"F18.opExtrude","CAP_EDGE",EDGE,{"disambiguationData":[OSD([sQuery(id+"F16.wireOp",EDGE,"E72")])],"isStart":false});
            var Q23;
            Q23=makeQuery(id+"F18.opExtrude","CAP_EDGE",EDGE,{"disambiguationData":[OSD([sQuery(id+"F16.wireOp",EDGE,"E70.top")])],"isStart":false});
            chamfer(context, id + "F26", {"entities" : qUnion([Q0, Q1, Q2, Q3, Q4, Q5, Q6, Q7, Q8, Q9, Q10, Q11, Q12, Q13, Q14, Q15, Q16, Q17, Q18, Q19, Q20, Q21, Q22, Q23]), "width" : 1 * mm, "tangentPropagation" : true});
        }
        {
            var Q0;
            {var subQ0=sQuery(id+"F0.wireOp",EDGE,"E0.bottom");Q0=makeQuery(id+"F17.boolean.opBoolean","MERGE",EDGE,{"derivedFrom":[makeQuery(id+"F13.boolean.opBoolean","MERGE",EDGE,{"derivedFrom":[makeQuery(id+"F1.opExtrude","CAP_EDGE",EDGE,{"disambiguationData":[OSD([subQ0])],"isStart":false}),makeQuery(id+"F13.opExtrude","SWEPT_EDGE",EDGE,{"disambiguationData":[OSD([sQuery(id+"F12.wireOp",EDGE,"E65"),sQuery(id+"F12.wireOp",EDGE,"E66")])]})]}),makeQuery(id+"F17.opExtrude","SWEPT_EDGE",EDGE,{"disambiguationData":[OSD([subQ0,sQuery(id+"F0.wireOp",EDGE,"E0.left"),sQuery(id+"F4.wireOp",EDGE,"E31"),sQuery(id+"F4.wireOp",EDGE,"E32")])]})]});}
            fillet(context, id + "F27", {"entities" : qUnion([Q0]), "radius" : 10 * mm, "tangentPropagation" : true, "allowEdgeOverflow" : false});
        }
        {
            var Q0;
            {var subQ0=sQuery(id+"F4.wireOp",EDGE,"E32");var subQ1=sQuery(id+"F0.wireOp",EDGE,"E0.left");Q0=makeQuery(id+"F17.boolean.opBoolean","MERGE",FACE,{"derivedFrom":[makeQuery(id+"F13.boolean.opBoolean","MERGE",FACE,{"derivedFrom":[makeQuery(id+"F6.boolean.opBoolean","MERGE",FACE,{"derivedFrom":[makeQuery(id+"F1.opExtrude","CAP_FACE",FACE,{"disambiguationData":[OSD([sQuery(id+"F0.wireOp",EDGE,"E0.bottom"),sQuery(id+"F0.wireOp",EDGE,"E0.top"),subQ1,sQuery(id+"F0.wireOp",EDGE,"E0.right")])],"isStart":false}),makeQuery(id+"F6.opExtrude","SWEPT_FACE",FACE,{"disambiguationData":[OSD([subQ0])]}),makeQuery(id+"F6.opExtrude","SWEPT_FACE",FACE,{"disambiguationData":[OSD([sQuery(id+"F4.wireOp",EDGE,"E33")])]})]}),makeQuery(id+"F13.opExtrude","SWEPT_FACE",FACE,{"disambiguationData":[OSD([sQuery(id+"F12.wireOp",EDGE,"E65")])]})]}),makeQuery(id+"F17.opExtrude","SWEPT_FACE",FACE,{"disambiguationData":[OSD([subQ1,sQuery(id+"F4.wireOp",EDGE,"E31"),subQ0])]})]});}
            var sketch = newSketch(context, id + "F28", { "sketchPlane" : qUnion([Q0])});
            skLineSegment(sketch, "E82.bottom", {"start": v(24.15, 24.63) * mm, "end": v(17.15, 24.63) * mm});
            skLineSegment(sketch, "E82.top", {"start": v(24.15, 31.63) * mm, "end": v(17.15, 31.63) * mm});
            skLineSegment(sketch, "E82.left", {"start": v(24.15, 24.63) * mm, "end": v(24.15, 31.63) * mm});
            skLineSegment(sketch, "E82.right", {"start": v(17.15, 24.63) * mm, "end": v(17.15, 31.63) * mm});
            skLineSegment(sketch, "E83.MirrorCS", {"start": v(-17.15, 24.63) * mm, "end": v(-17.15, 31.63) * mm});
            skLineSegment(sketch, "E84.MirrorCS", {"start": v(-24.15, 24.63) * mm, "end": v(-17.15, 24.63) * mm});
            skLineSegment(sketch, "E85.MirrorCS", {"start": v(-24.15, 24.63) * mm, "end": v(-24.15, 31.63) * mm});
            skLineSegment(sketch, "E86.MirrorCS", {"start": v(-24.15, 31.63) * mm, "end": v(-17.15, 31.63) * mm});
            skSolve(sketch);
        }
        {
            var Q0;
            Q0 = qSketchRegion(id + "F28", true);
            extrude(context, id + "F29", {"entities" : qUnion([Q0]), "depth" : 15 * mm});
        }
        {
            var Q0;
            Q0=makeQuery(id+"F29.opExtrude","SWEPT_EDGE",EDGE,{"disambiguationData":[OSD([sQuery(id+"F28.wireOp",EDGE,"E82.bottom"),sQuery(id+"F28.wireOp",EDGE,"E82.left")])]});
            var Q1;
            Q1=makeQuery(id+"F29.opExtrude","SWEPT_EDGE",EDGE,{"disambiguationData":[OSD([sQuery(id+"F28.wireOp",EDGE,"E82.top"),sQuery(id+"F28.wireOp",EDGE,"E82.left")])]});
            var Q2;
            Q2=makeQuery(id+"F29.opExtrude","SWEPT_EDGE",EDGE,{"disambiguationData":[OSD([sQuery(id+"F28.wireOp",EDGE,"E85.MirrorCS"),sQuery(id+"F28.wireOp",EDGE,"E86.MirrorCS")])]});
            var Q3;
            Q3=makeQuery(id+"F29.opExtrude","SWEPT_EDGE",EDGE,{"disambiguationData":[OSD([sQuery(id+"F28.wireOp",EDGE,"E84.MirrorCS"),sQuery(id+"F28.wireOp",EDGE,"E85.MirrorCS")])]});
            fillet(context, id + "F30", {"entities" : qUnion([Q0, Q1, Q2, Q3]), "radius" : 2.41 * mm, "tangentPropagation" : true, "allowEdgeOverflow" : false});
        }
        {
            var Q0;
            Q0=makeQuery(id+"F29.opExtrude","CAP_EDGE",EDGE,{"disambiguationData":[OSD([sQuery(id+"F28.wireOp",EDGE,"E85.MirrorCS")])],"isStart":false});
            var Q1;
            Q1=makeQuery(id+"F29.opExtrude","CAP_EDGE",EDGE,{"disambiguationData":[OSD([sQuery(id+"F28.wireOp",EDGE,"E82.left")])],"isStart":false});
            fillet(context, id + "F31", {"entities" : qUnion([Q0, Q1]), "radius" : 2.9 * mm, "tangentPropagation" : true, "allowEdgeOverflow" : false});
        }
        {
            var Q0;
            Q0=makeQuery(id+"F29.opExtrude","SWEPT_FACE",FACE,{"disambiguationData":[OSD([sQuery(id+"F28.wireOp",EDGE,"E82.right")])]});
            var sketch = newSketch(context, id + "F32", { "sketchPlane" : qUnion([Q0])});
            skLineSegment(sketch, "E87", {"start": v(-28.27, 73.63) * mm, "end": v(-28.27, 70.63) * mm});
            skArc(sketch, "E88", {"start": v(-28.27, 70.63) * mm, "mid": v(-26.77, 72.13) * mm, "end": v(-28.27, 73.63) * mm});
            skSolve(sketch);
        }
        {
            var Q0;
            Q0=makeQuery(id+"F29.opExtrude","SWEPT_FACE",FACE,{"disambiguationData":[OSD([sQuery(id+"F28.wireOp",EDGE,"E83.MirrorCS")])]});
            var sketch = newSketch(context, id + "F33", { "sketchPlane" : qUnion([Q0])});
            skLineSegment(sketch, "E89", {"start": v(27.47, 69.43) * mm, "end": v(27.47, 71.43) * mm});
            skArc(sketch, "E90", {"start": v(27.47, 71.43) * mm, "mid": v(26.47, 70.43) * mm, "end": v(27.47, 69.43) * mm});
            skSolve(sketch);
        }
        {
            var Q0;
            Q0=makeQuery(id+"F32.imprint","IMPRINT",FACE,{"disambiguationData":[TD([[makeQuery(id+"F32.imprint","IMPRINT",EDGE,{"derivedFrom":sQuery(id+"F32.wireOp",EDGE,"E87")}),1.0]])]});
            var Q1;
            Q1=sQuery(id+"F32.wireOp",EDGE,"E87");
            revolve(context, id + "F34", {"operationType" : NewBodyOperationType.ADD, "entities" : qUnion([Q0]), "axis" : qUnion([Q1]), "revolveType" : RevolveType.FULL});
        }
        {
            var Q0;
            Q0=makeQuery(id+"F33.imprint","IMPRINT",FACE,{"disambiguationData":[TD([[makeQuery(id+"F33.imprint","IMPRINT",EDGE,{"derivedFrom":sQuery(id+"F33.wireOp",EDGE,"E89")}),1.0]])]});
            var Q1;
            Q1=sQuery(id+"F33.wireOp",EDGE,"E89");
            revolve(context, id + "F35", {"operationType" : NewBodyOperationType.ADD, "entities" : qUnion([Q0]), "axis" : qUnion([Q1]), "revolveType" : RevolveType.FULL});
        }
    });
